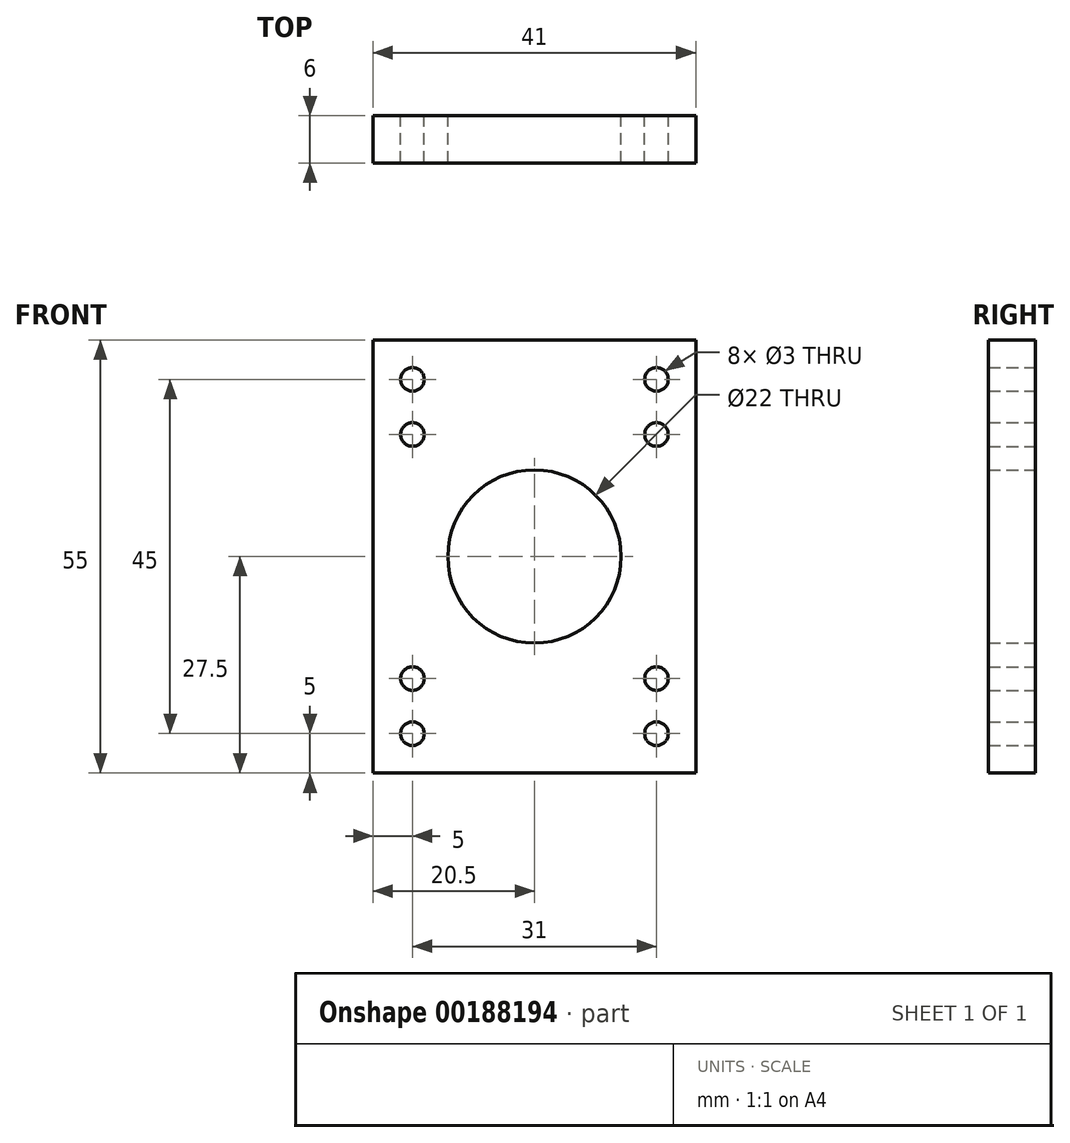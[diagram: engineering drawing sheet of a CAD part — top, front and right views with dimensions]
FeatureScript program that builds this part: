
annotation { "Feature Type Name" : "Feature", "Feature Type Description" : "" }
export const myFeature = defineFeature(function(context is Context, id is Id, definition is map)
    precondition{}
    {
        {
            var Q0;
            Q0=qCreatedBy(makeId("Front.planeOp"),FACE);
            var sketch = newSketch(context, id + "F0", { "sketchPlane" : qUnion([Q0])});
            skLineSegment(sketch, "E0.bottom", {"start": v(-20.5, -27.5) * mm, "end": v(20.5, -27.5) * mm});
            skLineSegment(sketch, "E0.top", {"start": v(-20.5, 27.5) * mm, "end": v(20.5, 27.5) * mm});
            skLineSegment(sketch, "E0.left", {"start": v(-20.5, -27.5) * mm, "end": v(-20.5, 27.5) * mm});
            skLineSegment(sketch, "E0.right", {"start": v(20.5, -27.5) * mm, "end": v(20.5, 27.5) * mm});
            skPoint(sketch, "E0.middle", {"position": v(0, 0) * mm});
            skCircle(sketch, "E1", {"center": v(-15.5, 22.5) * mm, "radius": 1.5 * mm});
            skLineSegment(sketch, "E2", {"start": v(-20.5, 0) * mm, "end": v(20.5, 0) * mm, "construction": true});
            skLineSegment(sketch, "E3", {"start": v(0, 27.5) * mm, "end": v(0, -27.5) * mm, "construction": true});
            skCircle(sketch, "E4.MirrorC", {"center": v(15.5, 22.5) * mm, "radius": 1.5 * mm});
            skCircle(sketch, "E5.MirrorC", {"center": v(-15.5, -22.5) * mm, "radius": 1.5 * mm});
            skCircle(sketch, "E6.MirrorC", {"center": v(15.5, -22.5) * mm, "radius": 1.5 * mm});
            skCircle(sketch, "E7", {"center": v(0, 0) * mm, "radius": 11 * mm});
            skLineSegment(sketch, "E8.bottom", {"start": v(-15.5, -15.5) * mm, "end": v(15.5, -15.5) * mm, "construction": true});
            skLineSegment(sketch, "E8.top", {"start": v(-15.5, 15.5) * mm, "end": v(15.5, 15.5) * mm, "construction": true});
            skLineSegment(sketch, "E8.left", {"start": v(-15.5, -15.5) * mm, "end": v(-15.5, 15.5) * mm, "construction": true});
            skLineSegment(sketch, "E8.right", {"start": v(15.5, -15.5) * mm, "end": v(15.5, 15.5) * mm, "construction": true});
            skCircle(sketch, "E9", {"center": v(-15.5, 15.5) * mm, "radius": 1.5 * mm});
            skCircle(sketch, "E10", {"center": v(15.5, 15.5) * mm, "radius": 1.5 * mm});
            skCircle(sketch, "E11", {"center": v(15.5, -15.5) * mm, "radius": 1.5 * mm});
            skCircle(sketch, "E12", {"center": v(-15.5, -15.5) * mm, "radius": 1.5 * mm});
            skSolve(sketch);
        }
        {
            var Q0;
            Q0=qSketchRegion(id+"F0",true);
            extrude(context, id + "F1", {"entities" : qUnion([Q0]), "depth" : 6 * mm});
        }
    });
